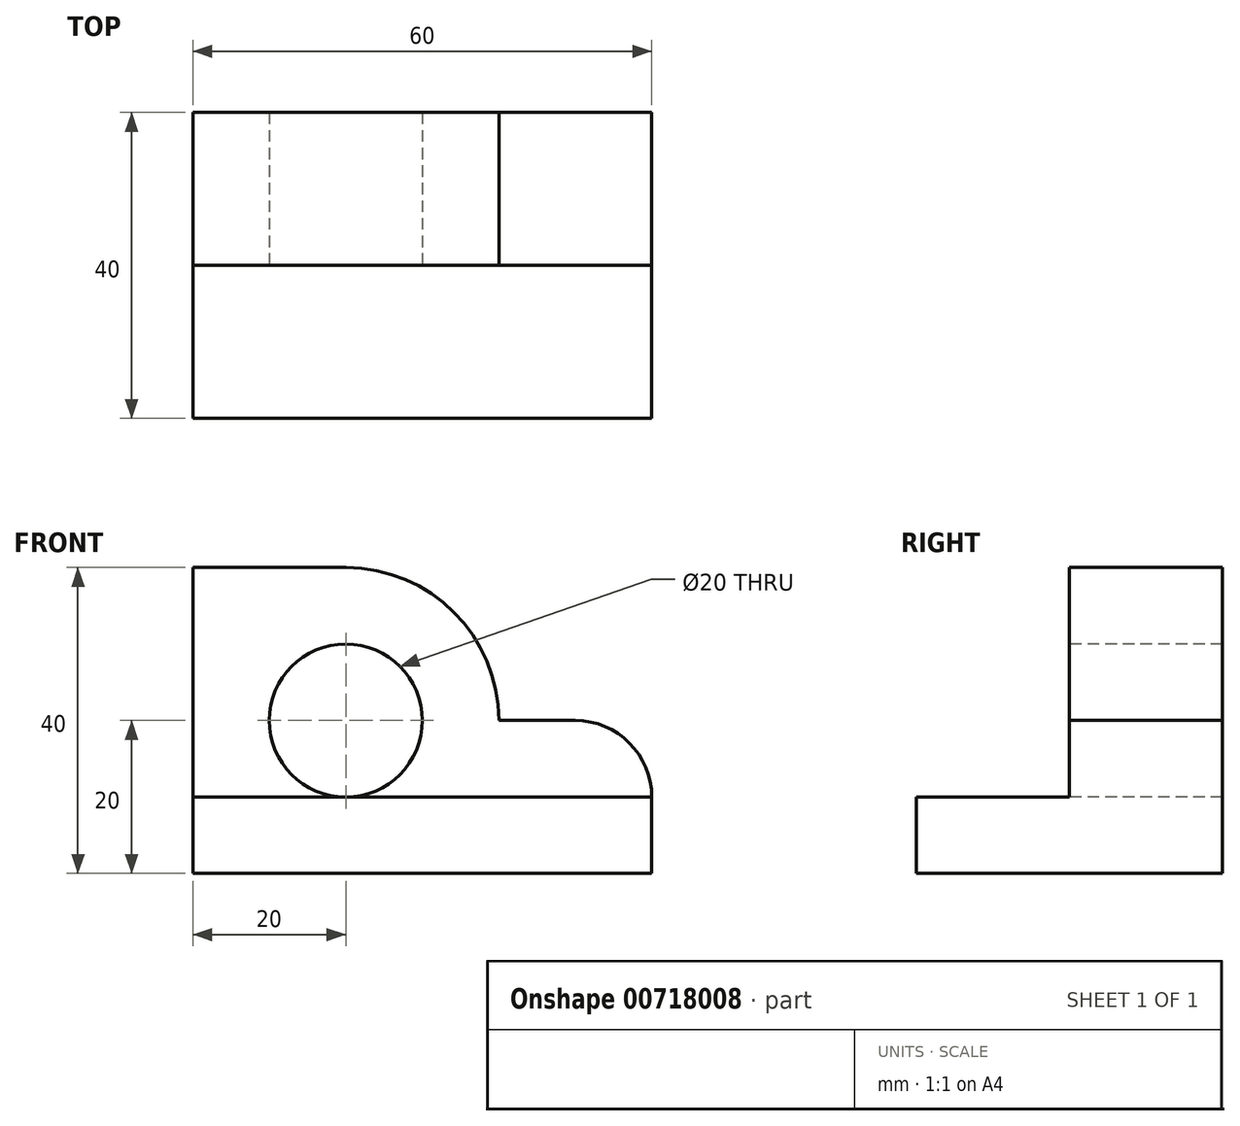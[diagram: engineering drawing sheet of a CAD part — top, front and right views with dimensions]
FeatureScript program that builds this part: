
annotation { "Feature Type Name" : "Feature", "Feature Type Description" : "" }
export const myFeature = defineFeature(function(context is Context, id is Id, definition is map)
    precondition{}
    {
        {
            var Q0;
            Q0=qCreatedBy(makeId("Top.planeOp"),FACE);
            var sketch = newSketch(context, id + "F0", { "sketchPlane" : qUnion([Q0])});
            skLineSegment(sketch, "E0", {"start": v(0, 0) * mm, "end": v(60, 0) * mm});
            skLineSegment(sketch, "E1", {"start": v(60, 0) * mm, "end": v(60, 40) * mm});
            skLineSegment(sketch, "E2", {"start": v(60, 40) * mm, "end": v(0, 40) * mm});
            skLineSegment(sketch, "E3", {"start": v(0, 40) * mm, "end": v(0, 0) * mm});
            skSolve(sketch);
        }
        {
            var Q0;
            Q0=makeQuery(id+"F0.imprint","IMPRINT",FACE,{"disambiguationData":[TD([[makeQuery(id+"F0.imprint","IMPRINT",EDGE,{"derivedFrom":sQuery(id+"F0.wireOp",EDGE,"E0")}),1.0]])]});
            extrude(context, id + "F1", {"entities" : qUnion([Q0]), "depth" : 40 * mm, "offsetDistance" : 25 * mm});
        }
        {
            var Q0;
            Q0=makeQuery(id+"F1.opExtrude","CAP_FACE",FACE,{"disambiguationData":[OSD([sQuery(id+"F0.wireOp",EDGE,"E0"),sQuery(id+"F0.wireOp",EDGE,"E1"),sQuery(id+"F0.wireOp",EDGE,"E2"),sQuery(id+"F0.wireOp",EDGE,"E3")])],"isStart":false});
            var sketch = newSketch(context, id + "F2", { "sketchPlane" : qUnion([Q0])});
            skLineSegment(sketch, "E4.bottom", {"start": v(60, 0) * mm, "end": v(0, 0) * mm});
            skLineSegment(sketch, "E4.top", {"start": v(60, 20) * mm, "end": v(0, 20) * mm});
            skLineSegment(sketch, "E4.left", {"start": v(60, 0) * mm, "end": v(60, 20) * mm});
            skLineSegment(sketch, "E4.right", {"start": v(0, 0) * mm, "end": v(0, 20) * mm});
            skSolve(sketch);
        }
        {
            var Q0;
            Q0=makeQuery(id+"F2.imprint","IMPRINT",FACE,{"disambiguationData":[TD([[makeQuery(id+"F2.imprint","IMPRINT",EDGE,{"derivedFrom":sQuery(id+"F2.wireOp",EDGE,"E4.bottom")}),1.0]])]});
            extrude(context, id + "F3", {"entities" : qUnion([Q0]), "operationType" : NewBodyOperationType.REMOVE, "oppositeDirection" : true, "depth" : 30 * mm, "offsetDistance" : 25 * mm});
        }
        {
            var Q0;
            Q0=makeQuery(id+"F3.boolean.opBoolean","COPY",FACE,{"derivedFrom":makeQuery(id+"F3.opExtrude","SWEPT_FACE",FACE,{"disambiguationData":[OSD([sQuery(id+"F2.wireOp",EDGE,"E4.top")])]})});
            var sketch = newSketch(context, id + "F4", { "sketchPlane" : qUnion([Q0])});
            skCircle(sketch, "E5", {"center": v(17.33, 20.6) * mm, "radius": 10 * mm});
            skSolve(sketch);
        }
        {
            var Q0;
            Q0=makeQuery(id+"F4.imprint","IMPRINT",FACE,{"disambiguationData":[TD([[makeQuery(id+"F4.imprint","IMPRINT",EDGE,{"derivedFrom":sQuery(id+"F4.wireOp",EDGE,"E5")}),1.0]])]});
            extrude(context, id + "F5", {"entities" : qUnion([Q0]), "operationType" : NewBodyOperationType.ADD, "oppositeDirection" : true, "depth" : 20 * mm, "offsetDistance" : 25 * mm});
        }
        {
            var Q0;
            Q0=makeQuery(id+"F3.boolean.opBoolean","COPY",FACE,{"derivedFrom":makeQuery(id+"F3.opExtrude","SWEPT_FACE",FACE,{"disambiguationData":[OSD([sQuery(id+"F2.wireOp",EDGE,"E4.top")])]})});
            var sketch = newSketch(context, id + "F6", { "sketchPlane" : qUnion([Q0])});
            skLineSegment(sketch, "E6", {"start": v(0, 10) * mm, "end": v(0, 20) * mm});
            skLineSegment(sketch, "E7", {"start": v(0, 20) * mm, "end": v(20, 20) * mm});
            skLineSegment(sketch, "E8", {"start": v(20, 20) * mm, "end": v(40, 20) * mm});
            skLineSegment(sketch, "E9", {"start": v(40, 20) * mm, "end": v(60, 20) * mm});
            skCircle(sketch, "E10", {"center": v(20, 20) * mm, "radius": 10 * mm});
            skArc(sketch, "E11", {"start": v(40, 20) * mm, "mid": v(20, 40) * mm, "end": v(0, 20) * mm});
            skArc(sketch, "E12", {"start": v(60, 10) * mm, "mid": v(57.07, 17.07) * mm, "end": v(50, 20) * mm});
            skSolve(sketch);
        }
        {
            var Q0;
            {var subQ0=sQuery(id+"F6.wireOp",EDGE,"E8");var subQ1=sQuery(id+"F6.wireOp",EDGE,"E7");var subQ2=makeQuery(id+"F6.imprint","INTERSECT",VERTEX,{"derivedFrom":[subQ1,subQ0]});Q0=makeQuery(id+"F6.imprint","IMPRINT",FACE,{"disambiguationData":[TD([[makeQuery(id+"F6.imprint","IMPRINT",EDGE,{"disambiguationData":[TD([[subQ2,1.0]])],"derivedFrom":subQ1}),1.0]])]});}
            var Q1;
            {var subQ0=sQuery(id+"F6.wireOp",EDGE,"E8");var subQ1=sQuery(id+"F6.wireOp",EDGE,"E7");var subQ2=makeQuery(id+"F6.imprint","INTERSECT",VERTEX,{"derivedFrom":[subQ1,subQ0]});Q1=makeQuery(id+"F6.imprint","IMPRINT",FACE,{"disambiguationData":[TD([[makeQuery(id+"F6.imprint","IMPRINT",EDGE,{"disambiguationData":[TD([[subQ2,1.0]])],"derivedFrom":subQ1}),-1.0]])]});}
            var Q2;
            {var subQ0=sQuery(id+"F6.wireOp",EDGE,"E11");var subQ1=sQuery(id+"F2.wireOp",EDGE,"E4.top");var subQ4=makeQuery(id+"F3.boolean.opBoolean","COPY",EDGE,{"derivedFrom":makeQuery(id+"F3.opExtrude","CAP_EDGE",EDGE,{"disambiguationData":[OSD([subQ1])],"isStart":true})});var subQ5=makeQuery(id+"F6.imprint","INTERSECT",VERTEX,{"derivedFrom":[subQ4,subQ0]});Q2=makeQuery(id+"F6.imprint","IMPRINT",FACE,{"disambiguationData":[TD([[makeQuery(id+"F6.imprint","IMPRINT",EDGE,{"disambiguationData":[TD([[subQ5,-1.0]])],"derivedFrom":subQ4}),1.0]])]});}
            var Q3;
            {var subQ4=sQuery(id+"F6.wireOp",EDGE,"E9");var subQ6=makeQuery(id+"F6.imprint","INTERSECT",VERTEX,{"derivedFrom":[subQ4,sQuery(id+"F6.wireOp",EDGE,"E12")]});Q3=makeQuery(id+"F6.imprint","IMPRINT",FACE,{"disambiguationData":[TD([[makeQuery(id+"F6.imprint","IMPRINT",EDGE,{"disambiguationData":[TD([[subQ6,1.0]])],"derivedFrom":subQ4}),1.0]])]});}
            extrude(context, id + "F7", {"entities" : qUnion([Q0, Q1, Q2, Q3]), "operationType" : NewBodyOperationType.REMOVE, "oppositeDirection" : true, "depth" : 20 * mm, "offsetDistance" : 25 * mm});
        }
        {
            var Q0;
            Q0=makeQuery(id+"F3.boolean.opBoolean","COPY",FACE,{"derivedFrom":makeQuery(id+"F3.opExtrude","SWEPT_FACE",FACE,{"disambiguationData":[OSD([sQuery(id+"F2.wireOp",EDGE,"E4.top")])]})});
            var sketch = newSketch(context, id + "F8", { "sketchPlane" : qUnion([Q0])});
            skArc(sketch, "E13", {"start": v(60, 10) * mm, "mid": v(57.07, 17.07) * mm, "end": v(50, 20) * mm});
            skSolve(sketch);
        }
        {
            var Q0;
            {var subQ0=sQuery(id+"F8.wireOp",EDGE,"E13");Q0=makeQuery(id+"F8.imprint","IMPRINT",FACE,{"disambiguationData":[TD([[makeQuery(id+"F8.imprint","IMPRINT",EDGE,{"derivedFrom":subQ0}),-1.0]])]});}
            extrude(context, id + "F9", {"entities" : qUnion([Q0]), "operationType" : NewBodyOperationType.REMOVE, "oppositeDirection" : true, "depth" : 20 * mm, "offsetDistance" : 25 * mm});
        }
    });
